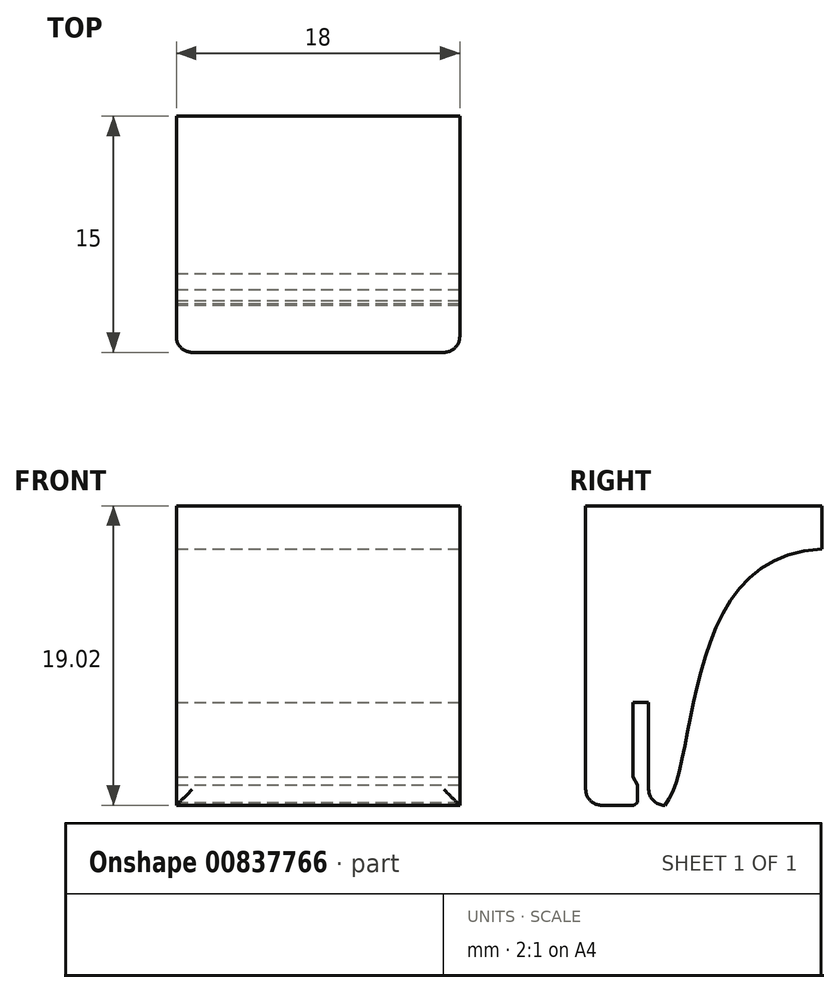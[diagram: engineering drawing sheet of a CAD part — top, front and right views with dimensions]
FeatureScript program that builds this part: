
annotation { "Feature Type Name" : "Feature", "Feature Type Description" : "" }
export const myFeature = defineFeature(function(context is Context, id is Id, definition is map)
    precondition{}
    {
        {
            var Q0;
            Q0=qCreatedBy(makeId("Front.planeOp"),FACE);
            var sketch = newSketch(context, id + "F0", { "sketchPlane" : qUnion([Q0])});
            skLineSegment(sketch, "E0", {"start": v(-85.3, 0) * mm, "end": v(115.65, 0) * mm, "construction": true});
            skLineSegment(sketch, "E1", {"start": v(0, 65.32) * mm, "end": v(0, -56.93) * mm, "construction": true});
            skLineSegment(sketch, "E2", {"start": v(-9, 0) * mm, "end": v(-9, 12.5) * mm});
            skLineSegment(sketch, "E3", {"start": v(-9, 12.5) * mm, "end": v(9, 12.48) * mm});
            skLineSegment(sketch, "E4", {"start": v(9, 12.48) * mm, "end": v(9, -6.52) * mm});
            skLineSegment(sketch, "E5", {"start": v(9, -6.52) * mm, "end": v(-9, -6.52) * mm});
            skLineSegment(sketch, "E6", {"start": v(-9, -6.52) * mm, "end": v(-9, 0) * mm});
            skSolve(sketch);
        }
        {
            var Q0;
            Q0 = qSketchRegion(id + "F0", true);
            extrude(context, id + "F1", {"entities" : qUnion([Q0]), "oppositeDirection" : true, "depth" : 15 * mm, "offsetDistance" : 25 * mm});
        }
        {
            var Q0;
            Q0=makeQuery(id+"F1.opExtrude","SWEPT_FACE",FACE,{"disambiguationData":[OSD([sQuery(id+"F0.wireOp",EDGE,"E4")])]});
            cPlane(context, id + "F2", {"entities" : qUnion([Q0]), "cplaneType" : CPlaneType.OFFSET, "offset" : 0 * mm, "width" : 150 * mm, "height" : 150 * mm});
        }
        {
            var Q0;
            Q0=qCreatedBy(id+"F2.planeOp",FACE);
            var sketch = newSketch(context, id + "F3", { "sketchPlane" : qUnion([Q0])});
            skLineSegment(sketch, "E7", {"start": v(3, -3.06) * mm, "end": v(3, -9.37) * mm, "construction": true});
            skLineSegment(sketch, "E8", {"start": v(3, 16.2) * mm, "end": v(4, 16.2) * mm, "construction": true});
            skLineSegment(sketch, "E9", {"start": v(4, -9.82) * mm, "end": v(18.21, -9.82) * mm, "construction": true});
            skLineSegment(sketch, "E10", {"start": v(3, -6.9) * mm, "end": v(3, 0) * mm});
            skLineSegment(sketch, "E11", {"start": v(3, 0) * mm, "end": v(4, 0) * mm});
            skLineSegment(sketch, "E12", {"start": v(4, 0) * mm, "end": v(4, -6.9) * mm});
            skLineSegment(sketch, "E13", {"start": v(4, -6.9) * mm, "end": v(3, -6.9) * mm});
            skLineSegment(sketch, "E14", {"start": v(15.56, -0.22) * mm, "end": v(15.56, -7.87) * mm});
            skLineSegment(sketch, "E15", {"start": v(15.56, -7.87) * mm, "end": v(4, -7.87) * mm});
            skLineSegment(sketch, "E16", {"start": v(4, -7.87) * mm, "end": v(4, -6.9) * mm});
            skLineSegment(sketch, "E17", {"start": v(3, -6.57) * mm, "end": v(3.29, -6.34) * mm});
            skLineSegment(sketch, "E18", {"start": v(3.29, -6.34) * mm, "end": v(3.29, -5.23) * mm});
            skLineSegment(sketch, "E19", {"start": v(3.29, -5.23) * mm, "end": v(3, -4.73) * mm});
            skFitSpline(sketch, "E20", {"points": [v(4, -6.9) * mm, v(15.3, 9.76) * mm], "startDerivative": vector(11.5, -1.69) * mm, "endDerivative": vector(31.74, 0.12) * mm});
            skLineSegment(sketch, "E21", {"start": v(15.55, 0.1) * mm, "end": v(15.3, 9.76) * mm});
            skLineSegment(sketch, "E22", {"start": v(15.56, -0.22) * mm, "end": v(15.55, 0.1) * mm});
            skSolve(sketch);
        }
        {
            var Q0;
            {var subQ0=sQuery(id+"F3.wireOp",EDGE,"E11");Q0=makeQuery(id+"F3.imprint","IMPRINT",FACE,{"disambiguationData":[TD([[makeQuery(id+"F3.imprint","IMPRINT",EDGE,{"derivedFrom":subQ0}),-1.0]])]});}
            var Q1;
            Q1=makeQuery(id+"F3.imprint","IMPRINT",FACE,{"disambiguationData":[TD([[makeQuery(id+"F3.imprint","IMPRINT",EDGE,{"derivedFrom":sQuery(id+"F3.wireOp",EDGE,"E14")}),-1.0]])]});
            extrude(context, id + "F4", {"entities" : qUnion([Q0, Q1]), "operationType" : NewBodyOperationType.REMOVE, "oppositeDirection" : true, "depth" : 19 * mm, "offsetDistance" : 25 * mm});
        }
        {
            var Q0;
            Q0=makeQuery(id+"F1.opExtrude","CAP_EDGE",EDGE,{"disambiguationData":[OSD([sQuery(id+"F0.wireOp",EDGE,"E2"),sQuery(id+"F0.wireOp",EDGE,"E6")])],"isStart":true});
            var Q1;
            Q1=makeQuery(id+"F1.opExtrude","CAP_EDGE",EDGE,{"disambiguationData":[OSD([sQuery(id+"F0.wireOp",EDGE,"E5")])],"isStart":true});
            var Q2;
            Q2=makeQuery(id+"F1.opExtrude","CAP_EDGE",EDGE,{"disambiguationData":[OSD([sQuery(id+"F0.wireOp",EDGE,"E4")])],"isStart":true});
            var Q3;
            Q3=makeQuery(id+"F4.boolean.opBoolean","INTERSECT",EDGE,{"derivedFrom":[makeQuery(id+"F1.opExtrude","SWEPT_FACE",FACE,{"disambiguationData":[OSD([sQuery(id+"F0.wireOp",EDGE,"E5")])]}),makeQuery(id+"F4.opExtrude","SWEPT_FACE",FACE,{"disambiguationData":[OSD([sQuery(id+"F3.wireOp",EDGE,"E12")])]})]});
            fillet(context, id + "F5", {"entities" : qUnion([Q0, Q1, Q2, Q3]), "radius" : 1 * mm, "tangentPropagation" : true, "allowEdgeOverflow" : false});
        }
    });
